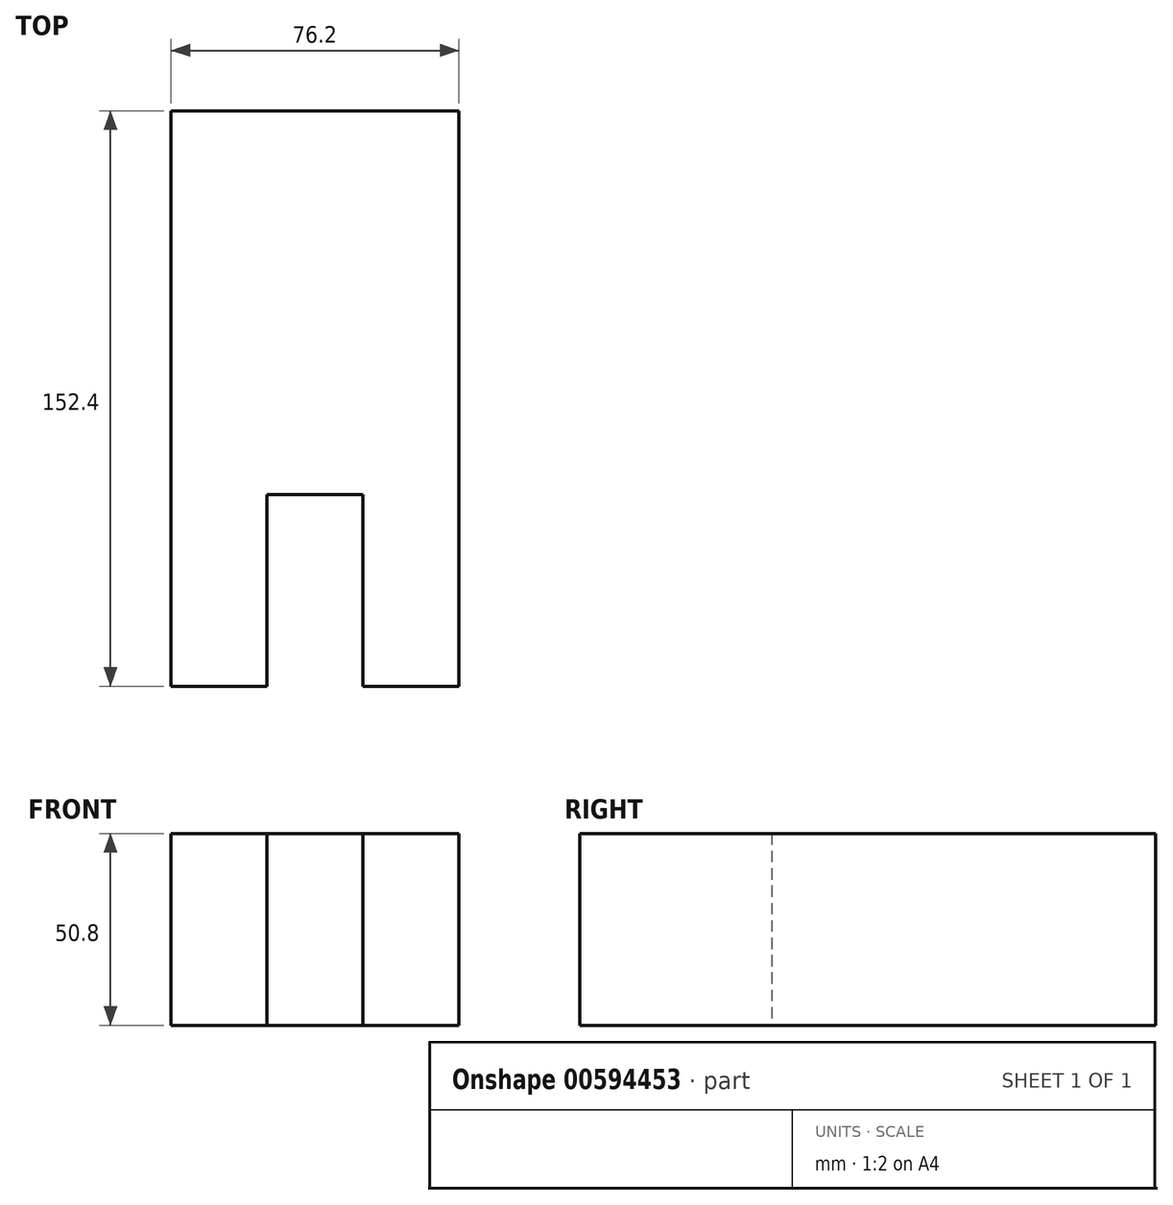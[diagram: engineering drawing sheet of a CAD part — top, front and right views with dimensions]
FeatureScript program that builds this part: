
annotation { "Feature Type Name" : "Feature", "Feature Type Description" : "" }
export const myFeature = defineFeature(function(context is Context, id is Id, definition is map)
    precondition{}
    {
        {
            var Q0;
            Q0=qCreatedBy(makeId("Top.planeOp"),FACE);
            var sketch = newSketch(context, id + "F0", { "sketchPlane" : qUnion([Q0])});
            skLineSegment(sketch, "E0", {"start": v(0, 0) * mm, "end": v(0, -152.4) * mm});
            skLineSegment(sketch, "E1", {"start": v(0, -152.4) * mm, "end": v(25.4, -152.4) * mm});
            skLineSegment(sketch, "E2", {"start": v(25.4, -152.4) * mm, "end": v(25.4, -101.6) * mm});
            skLineSegment(sketch, "E3", {"start": v(25.4, -101.6) * mm, "end": v(50.8, -101.6) * mm});
            skLineSegment(sketch, "E4", {"start": v(50.8, -101.6) * mm, "end": v(50.8, -152.4) * mm});
            skLineSegment(sketch, "E5", {"start": v(50.8, -152.4) * mm, "end": v(76.2, -152.4) * mm});
            skLineSegment(sketch, "E6", {"start": v(76.2, -152.4) * mm, "end": v(76.2, 0) * mm});
            skLineSegment(sketch, "E7", {"start": v(76.2, 0) * mm, "end": v(0, 0) * mm});
            skSolve(sketch);
        }
        {
            var Q0;
            Q0=makeQuery(id+"F0.imprint","IMPRINT",FACE,{"disambiguationData":[TD([[makeQuery(id+"F0.imprint","IMPRINT",EDGE,{"derivedFrom":sQuery(id+"F0.wireOp",EDGE,"E0")}),1.0]])]});
            extrude(context, id + "F1", {"entities" : qUnion([Q0]), "depth" : 50.8 * mm, "offsetDistance" : 25.4 * mm});
        }
    });
